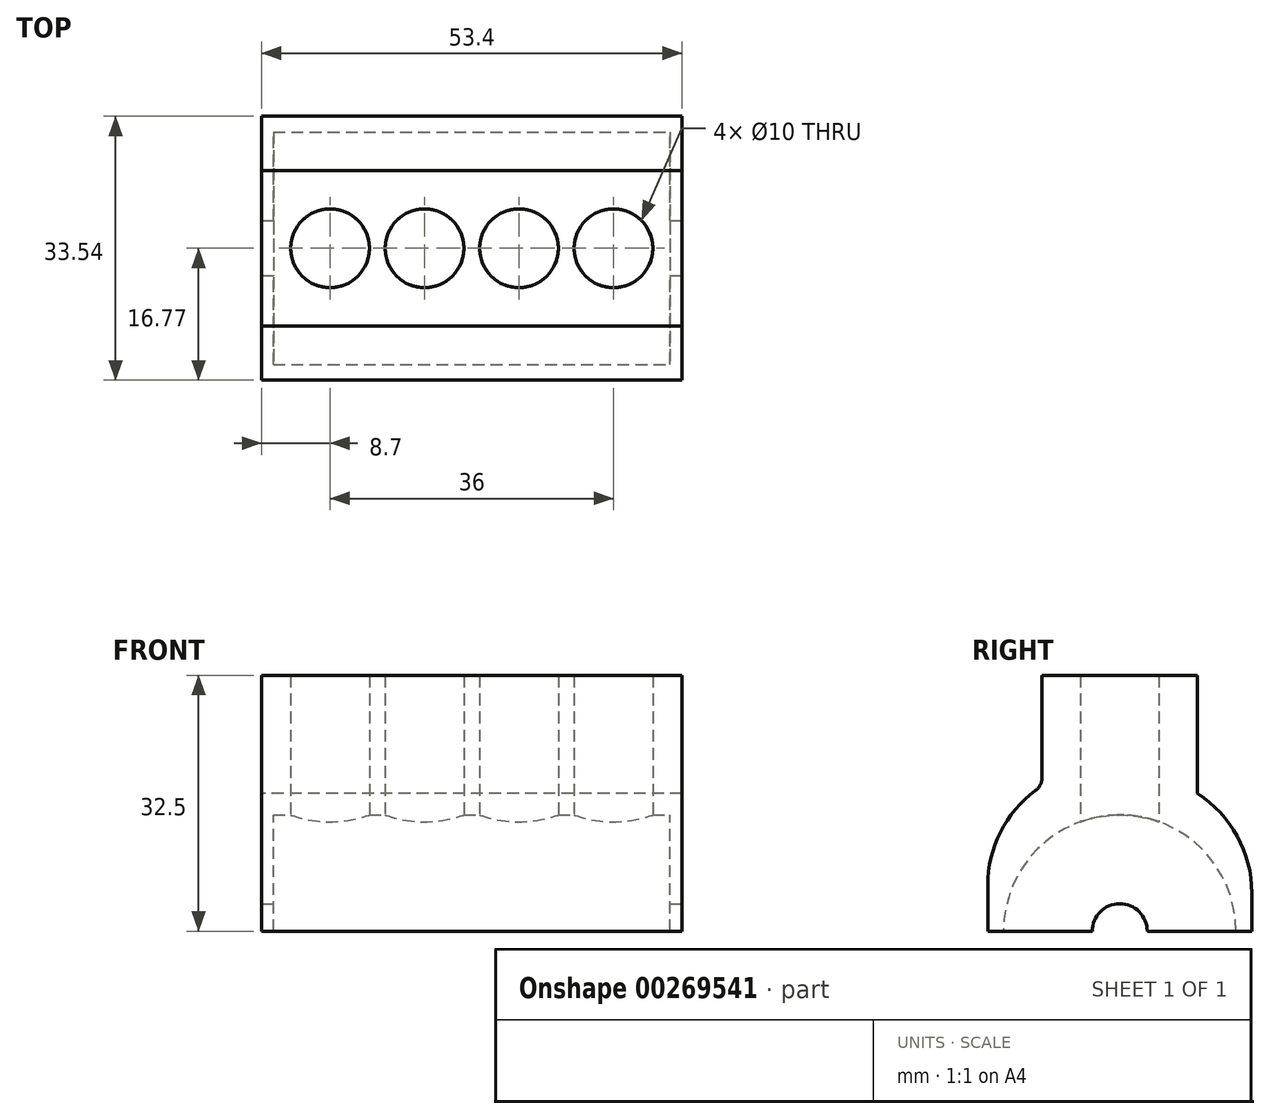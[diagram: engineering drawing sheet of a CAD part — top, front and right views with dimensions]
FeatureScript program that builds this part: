
annotation { "Feature Type Name" : "Feature", "Feature Type Description" : "" }
export const myFeature = defineFeature(function(context is Context, id is Id, definition is map)
    precondition{}
    {
        {
            var Q0;
            Q0=qCreatedBy(makeId("Top.planeOp"),FACE);
            var sketch = newSketch(context, id + "F0", { "sketchPlane" : qUnion([Q0])});
            skCircle(sketch, "E0", {"center": v(-6, 0) * mm, "radius": 5 * mm});
            skCircle(sketch, "E1", {"center": v(-18, 0) * mm, "radius": 5 * mm});
            skCircle(sketch, "E2", {"center": v(6, 0) * mm, "radius": 5 * mm});
            skCircle(sketch, "E3", {"center": v(18, 0) * mm, "radius": 5 * mm});
            skLineSegment(sketch, "E4.bottom", {"start": v(26.7, 9.88) * mm, "end": v(-26.7, 9.88) * mm});
            skLineSegment(sketch, "E4.top", {"start": v(26.7, -9.88) * mm, "end": v(-26.7, -9.88) * mm});
            skLineSegment(sketch, "E4.left", {"start": v(26.7, 9.88) * mm, "end": v(26.7, -9.88) * mm});
            skLineSegment(sketch, "E4.right", {"start": v(-26.7, 9.88) * mm, "end": v(-26.7, -9.88) * mm});
            skPoint(sketch, "E4.middle", {"position": v(0, 0) * mm});
            skSolve(sketch);
        }
        {
            var Q0;
            Q0 = qSketchRegion(id + "F0", true);
            extrude(context, id + "F1", {"entities" : qUnion([Q0]), "depth" : 15 * mm});
        }
        {
            var Q0;
            Q0=makeQuery(id+"F1.opExtrude","CAP_FACE",FACE,{"disambiguationData":[OSD([sQuery(id+"F0.wireOp",EDGE,"E0"),sQuery(id+"F0.wireOp",EDGE,"E1"),sQuery(id+"F0.wireOp",EDGE,"E2"),sQuery(id+"F0.wireOp",EDGE,"E3"),sQuery(id+"F0.wireOp",EDGE,"E4.bottom"),sQuery(id+"F0.wireOp",EDGE,"E4.top"),sQuery(id+"F0.wireOp",EDGE,"E4.left"),sQuery(id+"F0.wireOp",EDGE,"E4.right")])],"isStart":false});
            var sketch = newSketch(context, id + "F2", { "sketchPlane" : qUnion([Q0])});
            skLineSegment(sketch, "E5", {"start": v(26.7, 0) * mm, "end": v(-26.7, 0) * mm, "construction": true});
            skLineSegment(sketch, "E6", {"start": v(0, 9.88) * mm, "end": v(0, -9.88) * mm, "construction": true});
            skSolve(sketch);
        }
        {
            var Q0;
            Q0=makeQuery(id+"F1.opExtrude","CAP_FACE",FACE,{"disambiguationData":[OSD([sQuery(id+"F0.wireOp",EDGE,"E0"),sQuery(id+"F0.wireOp",EDGE,"E1"),sQuery(id+"F0.wireOp",EDGE,"E2"),sQuery(id+"F0.wireOp",EDGE,"E3"),sQuery(id+"F0.wireOp",EDGE,"E4.bottom"),sQuery(id+"F0.wireOp",EDGE,"E4.top"),sQuery(id+"F0.wireOp",EDGE,"E4.left"),sQuery(id+"F0.wireOp",EDGE,"E4.right")])],"isStart":true});
            var sketch = newSketch(context, id + "F3", { "sketchPlane" : qUnion([Q0])});
            skLineSegment(sketch, "E7.bottom", {"start": v(26.7, 16.77) * mm, "end": v(-26.7, 16.77) * mm});
            skLineSegment(sketch, "E7.top", {"start": v(26.7, -16.77) * mm, "end": v(-26.7, -16.77) * mm});
            skLineSegment(sketch, "E7.left", {"start": v(26.7, 16.77) * mm, "end": v(26.7, -16.77) * mm});
            skLineSegment(sketch, "E7.right", {"start": v(-26.7, 16.77) * mm, "end": v(-26.7, -16.77) * mm});
            skPoint(sketch, "E7.middle", {"position": v(0, 0) * mm});
            skSolve(sketch);
        }
        {
            var Q0;
            Q0 = qSketchRegion(id + "F3", true);
            extrude(context, id + "F4", {"entities" : qUnion([Q0]), "operationType" : NewBodyOperationType.ADD, "depth" : 17.5 * mm, "offsetDistance" : 25 * mm});
        }
        {
            var Q0;
            Q0=makeQuery(id+"F1.opExtrude","CAP_EDGE",EDGE,{"disambiguationData":[OSD([sQuery(id+"F0.wireOp",EDGE,"E4.bottom")])],"isStart":true});
            var Q1;
            Q1=makeQuery(id+"F1.opExtrude","CAP_EDGE",EDGE,{"disambiguationData":[OSD([sQuery(id+"F0.wireOp",EDGE,"E4.top")])],"isStart":true});
            fillet(context, id + "F5", {"entities" : qUnion([Q0, Q1]), "radius" : 2 * mm, "tangentPropagation" : true, "allowEdgeOverflow" : false});
        }
        {
            var Q0;
            Q0=makeQuery(id+"F4.opExtrude","CAP_EDGE",EDGE,{"disambiguationData":[OSD([sQuery(id+"F3.wireOp",EDGE,"E7.bottom")])],"isStart":true});
            var Q1;
            Q1=makeQuery(id+"F4.opExtrude","CAP_EDGE",EDGE,{"disambiguationData":[OSD([sQuery(id+"F3.wireOp",EDGE,"E7.top")])],"isStart":true});
            fillet(context, id + "F6", {"entities" : qUnion([Q0, Q1]), "radius" : 15 * mm, "tangentPropagation" : true, "allowEdgeOverflow" : false});
        }
        {
            var Q0;
            Q0=makeQuery(id+"F2.imprint","IMPRINT",FACE,{"disambiguationData":[TD([[makeQuery(id+"F2.imprint","IMPRINT",EDGE,{"derivedFrom":makeQuery(id+"F1.opExtrude","CAP_EDGE",EDGE,{"disambiguationData":[OSD([sQuery(id+"F0.wireOp",EDGE,"E1")])],"isStart":false})}),1.0]])]});
            var Q1;
            Q1=makeQuery(id+"F2.imprint","IMPRINT",FACE,{"disambiguationData":[TD([[makeQuery(id+"F2.imprint","IMPRINT",EDGE,{"derivedFrom":makeQuery(id+"F1.opExtrude","CAP_EDGE",EDGE,{"disambiguationData":[OSD([sQuery(id+"F0.wireOp",EDGE,"E0")])],"isStart":false})}),1.0]])]});
            var Q2;
            Q2=makeQuery(id+"F2.imprint","IMPRINT",FACE,{"disambiguationData":[TD([[makeQuery(id+"F2.imprint","IMPRINT",EDGE,{"derivedFrom":makeQuery(id+"F1.opExtrude","CAP_EDGE",EDGE,{"disambiguationData":[OSD([sQuery(id+"F0.wireOp",EDGE,"E2")])],"isStart":false})}),1.0]])]});
            var Q3;
            Q3=makeQuery(id+"F2.imprint","IMPRINT",FACE,{"disambiguationData":[TD([[makeQuery(id+"F2.imprint","IMPRINT",EDGE,{"derivedFrom":makeQuery(id+"F1.opExtrude","CAP_EDGE",EDGE,{"disambiguationData":[OSD([sQuery(id+"F0.wireOp",EDGE,"E3")])],"isStart":false})}),1.0]])]});
            extrude(context, id + "F7", {"entities" : qUnion([Q0, Q1, Q2, Q3]), "operationType" : NewBodyOperationType.REMOVE, "oppositeDirection" : true, "depth" : 44.27 * mm, "offsetDistance" : 25 * mm});
        }
        {
            var Q0;
            Q0=makeQuery(id+"F4.opExtrude","CAP_FACE",FACE,{"disambiguationData":[OSD([sQuery(id+"F3.wireOp",EDGE,"E7.bottom"),sQuery(id+"F3.wireOp",EDGE,"E7.top"),sQuery(id+"F3.wireOp",EDGE,"E7.left"),sQuery(id+"F3.wireOp",EDGE,"E7.right")])],"isStart":false});
            var sketch = newSketch(context, id + "F8", { "sketchPlane" : qUnion([Q0])});
            skLineSegment(sketch, "E8", {"start": v(-26.7, 0) * mm, "end": v(26.7, 0) * mm});
            skLineSegment(sketch, "E9", {"start": v(26.7, 0) * mm, "end": v(26.7, 0) * mm});
            skLineSegment(sketch, "E10", {"start": v(26.7, 0) * mm, "end": v(26.7, -3.5) * mm});
            skLineSegment(sketch, "E11", {"start": v(26.7, -3.5) * mm, "end": v(26.7, -3.5) * mm});
            skLineSegment(sketch, "E12", {"start": v(26.7, -3.5) * mm, "end": v(25.2, -3.5) * mm});
            skLineSegment(sketch, "E13", {"start": v(25.2, -3.5) * mm, "end": v(25.2, -3.5) * mm});
            skLineSegment(sketch, "E14", {"start": v(25.2, -14.77) * mm, "end": v(25.2, -3.5) * mm});
            skLineSegment(sketch, "E15", {"start": v(25.2, -14.77) * mm, "end": v(-25.2, -14.77) * mm});
            skLineSegment(sketch, "E16", {"start": v(-26.7, -3.5) * mm, "end": v(-26.7, 0) * mm});
            skLineSegment(sketch, "E17", {"start": v(-26.7, -3.5) * mm, "end": v(-25.2, -3.5) * mm});
            skLineSegment(sketch, "E18", {"start": v(-25.2, -3.5) * mm, "end": v(-25.2, -3.5) * mm});
            skLineSegment(sketch, "E19", {"start": v(-25.2, -14.77) * mm, "end": v(-25.2, -3.5) * mm});
            skSolve(sketch);
        }
        {
            var Q0;
            {var subQ0=sQuery(id+"F8.wireOp",EDGE,"E10");Q0=makeQuery(id+"F8.imprint","IMPRINT",FACE,{"disambiguationData":[TD([[makeQuery(id+"F8.imprint","IMPRINT",EDGE,{"derivedFrom":subQ0}),-1.0]])]});}
            var Q1;
            Q1=sQuery(id+"F8.wireOp",EDGE,"E8");
            revolve(context, id + "F9", {"operationType" : NewBodyOperationType.REMOVE, "entities" : qUnion([Q0]), "axis" : qUnion([Q1]), "revolveType" : RevolveType.FULL, "oppositeDirection" : true});
        }
    });
